# Revit family: CJ-46
name_source: partatom
category: Communication Devices
revit_build: Autodesk Revit 2014 (Build: 20140709_2115(x64)
units: mm (PartAtom-declared; Revit-internal decimal feet)

## types (1)
- Horn Loudspeaker
    100V Taps = 32.00 W
    70V Taps = 32.00 W
    Baffle Material = <By Category>
    Body Material = QF_Plastic - Black - Fine Textured
    Color = <By Category>
    Cost = 215.99 $
    Cost MSRP = 215.99 $
    Coverage Horizontal = 110.00°
    Coverage Vertical = 0.00°
    Depth = 0 "
    Description = WIDE DISPERSION REFLEX SOUND HORN, BLACK
    Dispersion Angle = 0.00°
    Enclosure Material = <By Category>
    Family Code (default) = LOUD SPEAKERS
    Grill Material = <By Category>
    Height = 0 "
    IQ Category = SPEAKERS
    Ingress Protection = TBD
    Manufacturer = ATLAS SOUND
    Manufacturer URL = https://www.atlasied.com
    Market = Commercial, Higher Education, Emergency
    MasterFormat = 27 41 13
    MaterFormat Title = SPEAKERS
    Model = CJ-46
    Mount Material = QF_Plastic - Black - Fine Textured
    OmniClass Number = 23-37 17 13 19
    OmniClass Title = SPEAKERS
    Pitch = 0.00°
    Product Documentation Link = https://www.atlasied.com
    Product Page URL = https://www.atlasied.com
    Rotation = 0.00°
    SPL Max = 107
    ScheduleType |RF| = AtlasIED Master
    Speaker Dispersion = 120.00°
    Transformer Option = Yes
    Vertical Symmetry = Yes
    Warranty = 5 Years
    Weight Product = 14.5
    Width = 0 "

## geometry (parser evidence)
native form markers: Blend x2, Sweep x2
no freeform markers — native parametric forms only
